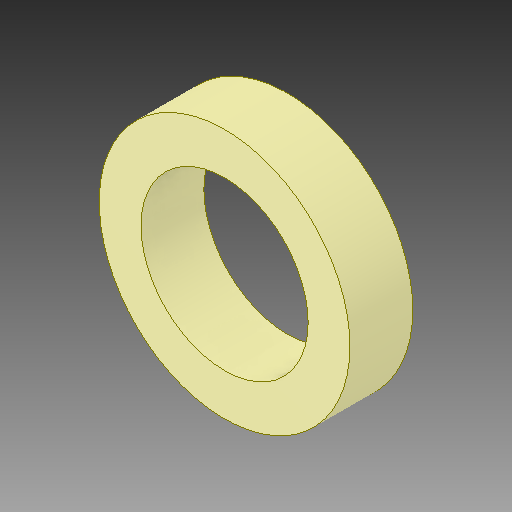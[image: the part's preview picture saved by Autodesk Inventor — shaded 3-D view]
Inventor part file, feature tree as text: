
AUTODESK INVENTOR PART (.ipt)
format: ipt  version: 2019 (Build 230136000, 136)  size: 97,792 bytes
history: native  units: in
note: dims shown in document units (in); Inventor stores cm internally (conversion verified against a paired STEP export)
features: revolve x1
ambient origin geometry x8: Origin, YZ Plane, XZ Plane, XY Plane, X Axis, Y Axis, Z Axis, Center Point
bodies: Solid1 (feature_tree)
feature tree (1):
  revolve  "Revolve1"  [1 undecoded]
note: 1 required parameter value undecoded (feature->parameter linkage not recoverable at this tier; creation-order binding heuristic only, values carry confidence <= 0.55)
